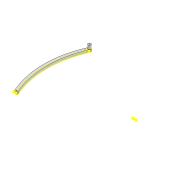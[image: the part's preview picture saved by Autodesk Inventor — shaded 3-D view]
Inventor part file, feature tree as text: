
AUTODESK INVENTOR PART (.ipt)
format: ipt  version: 2022 (Build 260153000, 153)  size: 126,464 bytes
history: native  units: mm
features: sketch x3, extrude x2, projected_geometry x2, fillet x1
ambient origin geometry x8: Origin, YZ Plane, XZ Plane, XY Plane, X Axis, Y Axis, Z Axis, Center Point
bodies: Solid1 (feature_tree)
feature tree (8):
  extrude  "Extrusion1"  Depth=10.0mm
  extrude  "Extrusion2"  Depth=8.0mm
  fillet  "Fillet1"  Radius=8.0mm
  sketch  "Sketch3"  dims[d12=10.0mm d13=12.0mm d14=0.0mm d18=300.0mm d19=300.0mm d20=4.0mm]
  sketch  "Sketch1"  dims[d0=244.795mm d1=10.0mm]
  sketch  "Sketch2"  dims[d2=3.0mm d3=3.0mm d4=8.0mm d5=0.0mm]
  projected_geometry  "Projected Loop1"
  projected_geometry  "Projected Loop2"
